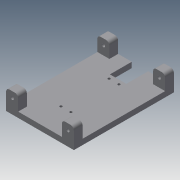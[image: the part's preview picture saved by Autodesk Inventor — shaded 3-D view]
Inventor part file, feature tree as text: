
AUTODESK INVENTOR PART (.ipt)
format: ipt  version: 2014 SP1 (Build 180222100, 222)  size: 148,480 bytes
history: native  units: in
note: dims shown in document units (in); Inventor stores cm internally (conversion verified against a paired STEP export)
features: extrude x3, sketch x2, fillet x1, pattern_linear x1
ambient origin geometry x8: Origin, YZ Plane, XZ Plane, XY Plane, X Axis, Y Axis, Z Axis, Center Point
bodies: Solid1 (feature_tree)
feature tree (7):
  extrude  "Extrusion1"  Depth=0.1969in
  extrude  "Extrusion4"  Depth=2.0079in
  extrude  "Extrusion5"  Depth=2.0079in
  fillet  "Fillet1"  Radius=0.1772in
  pattern_linear  "Rectangular Pattern4"  Spacing1=0.1772in  [1 undecoded]
  sketch  "Sketch4"  dims[d2=0.1969in d3=0.0in d4=0.0886in]
  sketch  "Sketch5"  dims[d5=0.0886in d6=0.8661in d7=0.8661in d8=0.1772in d9=0.1772in d28=0.4331in d29=0.315in d30=0.0in d31=0.7874in d32=0.5315in d33=0.0in d34=0.1181in d35=0.2165in d36=0.2165in d37=0.315in d38=0.0in d45=0.7874in d46=0.1181in d55=0.7874in d57=3.2874in d58=0.7874in d60=2.0079in]
note: 1 required parameter value undecoded (feature->parameter linkage not recoverable at this tier; creation-order binding heuristic only, values carry confidence <= 0.55)
